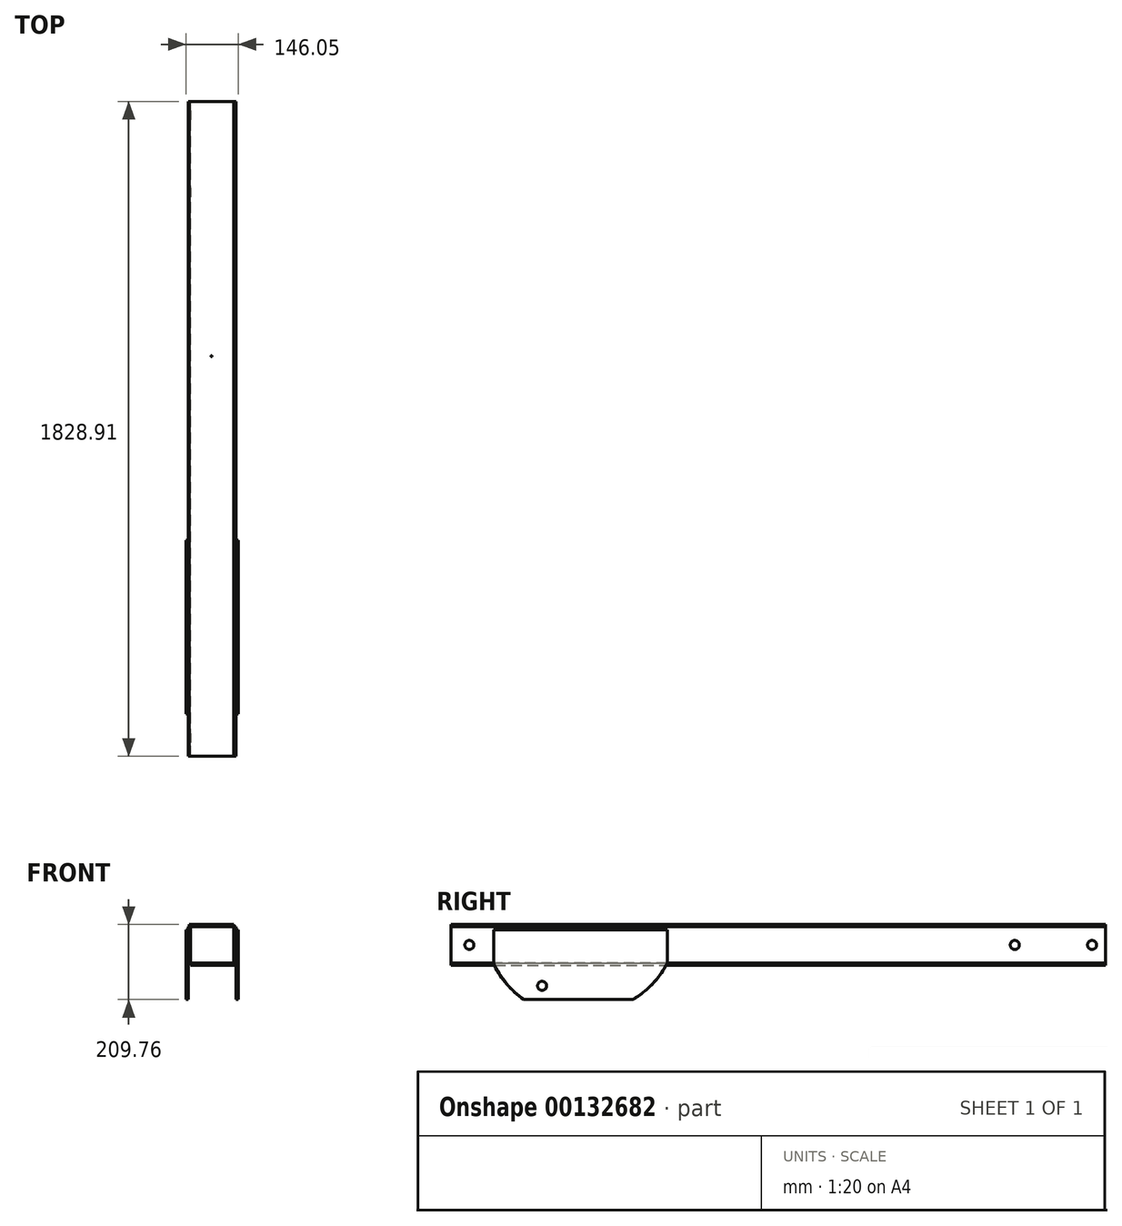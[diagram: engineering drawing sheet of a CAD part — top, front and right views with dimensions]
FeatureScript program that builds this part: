
annotation { "Feature Type Name" : "Feature", "Feature Type Description" : "" }
export const myFeature = defineFeature(function(context is Context, id is Id, definition is map)
    precondition{}
    {
        {
            var Q0;
            Q0=qCreatedBy(makeId("Right.planeOp"),FACE);
            var sketch = newSketch(context, id + "F0", { "sketchPlane" : qUnion([Q0])});
            skLineSegment(sketch, "E0.bottom", {"start": v(-870.5, -212.75) * mm, "end": v(958.3, -212.75) * mm});
            skLineSegment(sketch, "E0.top", {"start": v(-870.5, -314.35) * mm, "end": v(958.3, -314.35) * mm});
            skLineSegment(sketch, "E0.left", {"start": v(-870.5, -212.75) * mm, "end": v(-870.5, -314.35) * mm});
            skLineSegment(sketch, "E0.right", {"start": v(958.3, -212.75) * mm, "end": v(958.3, -314.35) * mm});
            skLineSegment(sketch, "E1.bottom", {"start": v(-667.3, -314.35) * mm, "end": v(-362.5, -314.35) * mm});
            skLineSegment(sketch, "E1.top", {"start": v(-667.3, -415.95) * mm, "end": v(-362.5, -415.95) * mm});
            skLineSegment(sketch, "E1.left", {"start": v(-667.3, -314.35) * mm, "end": v(-667.3, -415.95) * mm});
            skLineSegment(sketch, "E1.right", {"start": v(-362.5, -314.35) * mm, "end": v(-362.5, -415.95) * mm});
            skCircle(sketch, "E2", {"center": v(-616.5, -377.85) * mm, "radius": 12.7 * mm});
            skCircle(sketch, "E3", {"center": v(-819.7, -263.55) * mm, "radius": 12.7 * mm});
            skPoint(sketch, "E3.centerSnap0", {"position": v(-870.5, -263.55) * mm});
            skArc(sketch, "E4", {"start": v(-752, -314.35) * mm, "mid": v(-716.38, -370.76) * mm, "end": v(-667.3, -415.95) * mm});
            skArc(sketch, "E5", {"start": v(-362.5, -415.95) * mm, "mid": v(-307.51, -371.85) * mm, "end": v(-266.76, -314.35) * mm});
            skLineSegment(sketch, "E6.bottom", {"start": v(-752, -314.35) * mm, "end": v(-266.81, -314.35) * mm});
            skLineSegment(sketch, "E6.top", {"start": v(-752, -220.9) * mm, "end": v(-266.81, -220.9) * mm});
            skLineSegment(sketch, "E6.left", {"start": v(-752, -314.35) * mm, "end": v(-752, -220.9) * mm});
            skLineSegment(sketch, "E6.right", {"start": v(-266.81, -314.35) * mm, "end": v(-266.81, -220.9) * mm});
            skCircle(sketch, "E7", {"center": v(920.2, -263.55) * mm, "radius": 12.7 * mm});
            skPoint(sketch, "E7.centerSnap0", {"position": v(958.3, -263.55) * mm});
            skCircle(sketch, "E8", {"center": v(704.3, -263.55) * mm, "radius": 12.7 * mm});
            skSolve(sketch);
        }
        {
            var Q0;
            Q0=makeQuery(id+"F0.imprint","IMPRINT",FACE,{"disambiguationData":[TD([[makeQuery(id+"F0.imprint","IMPRINT",EDGE,{"derivedFrom":sQuery(id+"F0.wireOp",EDGE,"E0.bottom")}),-1.0]])]});
            var Q1;
            Q1=makeQuery(id+"F0.imprint","IMPRINT",FACE,{"disambiguationData":[TD([[makeQuery(id+"F0.imprint","IMPRINT",EDGE,{"derivedFrom":sQuery(id+"F0.wireOp",EDGE,"E6.top")}),-1.0]])]});
            extrude(context, id + "F1", {"entities" : qUnion([Q0, Q1]), "oppositeDirection" : true, "depth" : 6.35 * mm});
        }
        {
            var Q0;
            Q0=makeQuery(id+"F0.imprint","IMPRINT",FACE,{"disambiguationData":[TD([[makeQuery(id+"F0.imprint","IMPRINT",EDGE,{"derivedFrom":sQuery(id+"F0.wireOp",EDGE,"E6.top")}),-1.0]])]});
            var Q1;
            {var subQ0=sQuery(id+"F0.wireOp",EDGE,"E1.left");Q1=makeQuery(id+"F0.imprint","IMPRINT",FACE,{"disambiguationData":[TD([[makeQuery(id+"F0.imprint","IMPRINT",EDGE,{"derivedFrom":subQ0}),-1.0]])]});}
            var Q2;
            Q2=makeQuery(id+"F0.imprint","IMPRINT",FACE,{"disambiguationData":[TD([[makeQuery(id+"F0.imprint","IMPRINT",EDGE,{"derivedFrom":sQuery(id+"F0.wireOp",EDGE,"E1.top")}),1.0]])]});
            var Q3;
            {var subQ4=sQuery(id+"F0.wireOp",EDGE,"E1.right");Q3=makeQuery(id+"F0.imprint","IMPRINT",FACE,{"disambiguationData":[TD([[makeQuery(id+"F0.imprint","IMPRINT",EDGE,{"derivedFrom":subQ4}),1.0]])]});}
            extrude(context, id + "F2", {"entities" : qUnion([Q0, Q1, Q2, Q3]), "operationType" : NewBodyOperationType.ADD, "depth" : 6.35 * mm, "hasSecondDirection" : true, "secondDirectionOppositeDirection" : true, "secondDirectionDepth" : 0.03 * mm});
        }
        {
            var Q0;
            Q0=makeQuery(id+"F1.opExtrude","SWEPT_FACE",FACE,{"disambiguationData":[OSD([sQuery(id+"F0.wireOp",EDGE,"E0.bottom")])]});
            var sketch = newSketch(context, id + "F3", { "sketchPlane" : qUnion([Q0])});
            skLineSegment(sketch, "E9.bottom", {"start": v(-3.18, -870.5) * mm, "end": v(-130.18, -870.5) * mm});
            skLineSegment(sketch, "E9.top", {"start": v(-3.18, 958.3) * mm, "end": v(-130.18, 958.3) * mm});
            skLineSegment(sketch, "E9.left", {"start": v(-3.18, -870.5) * mm, "end": v(-3.18, 958.3) * mm});
            skLineSegment(sketch, "E9.right", {"start": v(-130.18, -870.5) * mm, "end": v(-130.18, 958.3) * mm});
            skSolve(sketch);
        }
        {
            var Q0;
            {var subQ2=sQuery(id+"F3.wireOp",EDGE,"E9.right");Q0=makeQuery(id+"F3.imprint","IMPRINT",FACE,{"disambiguationData":[TD([[makeQuery(id+"F3.imprint","IMPRINT",EDGE,{"derivedFrom":subQ2}),-1.0]])]});}
            extrude(context, id + "F4", {"entities" : qUnion([Q0]), "operationType" : NewBodyOperationType.ADD, "depth" : 6.35 * mm, "hasSecondDirection" : true, "secondDirectionOppositeDirection" : true, "secondDirectionDepth" : 0.03 * mm});
        }
        {
            var Q0;
            Q0=makeQuery(id+"F4.opExtrude","SWEPT_FACE",FACE,{"disambiguationData":[OSD([sQuery(id+"F3.wireOp",EDGE,"E9.right")])]});
            var sketch = newSketch(context, id + "F5", { "sketchPlane" : qUnion([Q0])});
            skLineSegment(sketch, "E10.bottom", {"start": v(870.5, -212.77) * mm, "end": v(-958.42, -212.77) * mm});
            skLineSegment(sketch, "E10.top", {"start": v(870.5, -314.26) * mm, "end": v(-958.42, -314.26) * mm});
            skLineSegment(sketch, "E10.left", {"start": v(870.5, -212.77) * mm, "end": v(870.5, -314.26) * mm});
            skLineSegment(sketch, "E10.right", {"start": v(-958.42, -212.77) * mm, "end": v(-958.42, -314.26) * mm});
            skCircle(sketch, "E11", {"center": v(-920.32, -263.52) * mm, "radius": 12.7 * mm});
            skPoint(sketch, "E11.centerSnap0", {"position": v(-958.42, -263.52) * mm});
            skCircle(sketch, "E12", {"center": v(819.7, -263.52) * mm, "radius": 12.7 * mm});
            skPoint(sketch, "E12.centerSnap0", {"position": v(870.5, -263.52) * mm});
            skCircle(sketch, "E13", {"center": v(-704.42, -263.46) * mm, "radius": 12.7 * mm});
            skSolve(sketch);
        }
        {
            var Q0;
            Q0=makeQuery(id+"F5.imprint","IMPRINT",FACE,{"disambiguationData":[TD([[makeQuery(id+"F5.imprint","IMPRINT",EDGE,{"derivedFrom":sQuery(id+"F5.wireOp",EDGE,"E10.top")}),-1.0]])]});
            extrude(context, id + "F6", {"entities" : qUnion([Q0]), "operationType" : NewBodyOperationType.ADD, "depth" : 3.17 * mm, "hasSecondDirection" : true, "secondDirectionOppositeDirection" : true, "secondDirectionDepth" : 3.17 * mm});
        }
        {
            var Q0;
            Q0=makeQuery(id+"F6.opExtrude","SWEPT_FACE",FACE,{"disambiguationData":[OSD([sQuery(id+"F5.wireOp",EDGE,"E10.top")])]});
            var sketch = newSketch(context, id + "F7", { "sketchPlane" : qUnion([Q0])});
            skLineSegment(sketch, "E14.bottom", {"start": v(-130.18, 870.5) * mm, "end": v(-3.18, 870.5) * mm});
            skLineSegment(sketch, "E14.top", {"start": v(-130.17, -958.3) * mm, "end": v(-3.17, -958.3) * mm});
            skLineSegment(sketch, "E14.left", {"start": v(-130.18, 870.5) * mm, "end": v(-130.18, -958.3) * mm});
            skLineSegment(sketch, "E14.right", {"start": v(-3.18, 870.5) * mm, "end": v(-3.17, -958.3) * mm});
            skSolve(sketch);
        }
        {
            var Q0;
            {var subQ3=sQuery(id+"F7.wireOp",EDGE,"E14.right");Q0=makeQuery(id+"F7.imprint","IMPRINT",FACE,{"disambiguationData":[TD([[makeQuery(id+"F7.imprint","IMPRINT",EDGE,{"derivedFrom":subQ3}),-1.0]])]});}
            extrude(context, id + "F8", {"entities" : qUnion([Q0]), "operationType" : NewBodyOperationType.ADD, "depth" : 6.35 * mm, "hasSecondDirection" : true, "secondDirectionOppositeDirection" : true, "secondDirectionDepth" : 0.03 * mm});
        }
        {
            var Q0;
            Q0=makeQuery(id+"F6.opExtrude","CAP_FACE",FACE,{"disambiguationData":[OSD([sQuery(id+"F5.wireOp",EDGE,"E10.bottom"),sQuery(id+"F5.wireOp",EDGE,"E10.top"),sQuery(id+"F5.wireOp",EDGE,"E10.left"),sQuery(id+"F5.wireOp",EDGE,"E10.right"),sQuery(id+"F5.wireOp",EDGE,"E11"),sQuery(id+"F5.wireOp",EDGE,"E12")])],"isStart":false});
            var sketch = newSketch(context, id + "F9", { "sketchPlane" : qUnion([Q0])});
            skLineSegment(sketch, "E15.bottom", {"start": v(266.66, -221.05) * mm, "end": v(752.84, -221.05) * mm});
            skLineSegment(sketch, "E15.top", {"start": v(266.66, -314.26) * mm, "end": v(752.84, -314.26) * mm});
            skLineSegment(sketch, "E15.left", {"start": v(266.66, -221.05) * mm, "end": v(266.66, -314.26) * mm});
            skLineSegment(sketch, "E15.right", {"start": v(752.84, -221.05) * mm, "end": v(752.84, -314.26) * mm});
            skLineSegment(sketch, "E16.bottom", {"start": v(362.73, -314.26) * mm, "end": v(667.5, -314.26) * mm});
            skLineSegment(sketch, "E16.top", {"start": v(362.73, -416.16) * mm, "end": v(667.5, -416.16) * mm});
            skLineSegment(sketch, "E16.left", {"start": v(362.73, -314.26) * mm, "end": v(362.73, -416.16) * mm});
            skLineSegment(sketch, "E16.right", {"start": v(667.5, -314.26) * mm, "end": v(667.5, -416.16) * mm});
            skArc(sketch, "E17", {"start": v(667.5, -416.16) * mm, "mid": v(716.95, -370.89) * mm, "end": v(752.84, -314.26) * mm});
            skArc(sketch, "E18", {"start": v(266.66, -314.26) * mm, "mid": v(307.53, -371.96) * mm, "end": v(362.73, -416.16) * mm});
            skCircle(sketch, "E19", {"center": v(616.73, -377.8) * mm, "radius": 12.7 * mm});
            skSolve(sketch);
        }
        {
            var Q0;
            Q0=makeQuery(id+"F9.imprint","IMPRINT",FACE,{"disambiguationData":[TD([[makeQuery(id+"F9.imprint","IMPRINT",EDGE,{"derivedFrom":sQuery(id+"F9.wireOp",EDGE,"E15.bottom")}),-1.0]])]});
            var Q1;
            {var subQ2=sQuery(id+"F9.wireOp",EDGE,"E16.left");Q1=makeQuery(id+"F9.imprint","IMPRINT",FACE,{"disambiguationData":[TD([[makeQuery(id+"F9.imprint","IMPRINT",EDGE,{"derivedFrom":subQ2}),-1.0]])]});}
            var Q2;
            Q2=makeQuery(id+"F9.imprint","IMPRINT",FACE,{"disambiguationData":[TD([[makeQuery(id+"F9.imprint","IMPRINT",EDGE,{"derivedFrom":sQuery(id+"F9.wireOp",EDGE,"E16.top")}),1.0]])]});
            var Q3;
            {var subQ2=sQuery(id+"F9.wireOp",EDGE,"E16.right");Q3=makeQuery(id+"F9.imprint","IMPRINT",FACE,{"disambiguationData":[TD([[makeQuery(id+"F9.imprint","IMPRINT",EDGE,{"derivedFrom":subQ2}),1.0]])]});}
            extrude(context, id + "F10", {"entities" : qUnion([Q0, Q1, Q2, Q3]), "operationType" : NewBodyOperationType.ADD, "depth" : 6.35 * mm});
        }
        {
            var Q0;
            Q0=makeQuery(id+"F4.opExtrude","CAP_FACE",FACE,{"disambiguationData":[OSD([sQuery(id+"F0.wireOp",EDGE,"E0.bottom"),sQuery(id+"F3.wireOp",EDGE,"E9.bottom"),sQuery(id+"F3.wireOp",EDGE,"E9.top"),sQuery(id+"F3.wireOp",EDGE,"E9.right")])],"isStart":false});
            var sketch = newSketch(context, id + "F11", { "sketchPlane" : qUnion([Q0])});
            skLineSegment(sketch, "E20", {"start": v(-68.26, -870.5) * mm, "end": v(-68.26, 247.1) * mm, "construction": true});
            skPoint(sketch, "E21", {"position": v(-68.26, 247.1) * mm});
            skSolve(sketch);
        }
        {
            var Q0;
            Q0=sQuery(id+"F11.wireOp",VERTEX,"E21");
            var Q1;
            Q1=makeQuery(id+"F1.opExtrude","SWEPT_BODY",BODY,{"disambiguationData":[OSD([sQuery(id+"F0.wireOp",EDGE,"E0.bottom"),sQuery(id+"F0.wireOp",EDGE,"E0.top"),sQuery(id+"F0.wireOp",EDGE,"E0.left"),sQuery(id+"F0.wireOp",EDGE,"E0.right"),sQuery(id+"F0.wireOp",EDGE,"E3"),sQuery(id+"F0.wireOp",EDGE,"E6.bottom"),sQuery(id+"F0.wireOp",EDGE,"E7"),sQuery(id+"F0.wireOp",EDGE,"E8")])]});
            hole(context, id + "F12", {"style" : HoleStyle.SIMPLE, "endStyle" : HoleEndStyle.THROUGH, "holeDiameter" : 3.17 * mm, "startFromSketch" : true, "locations" : qUnion([Q0]), "scope" : qUnion([Q1]), "isTappedThrough" : true});
        }
    });
